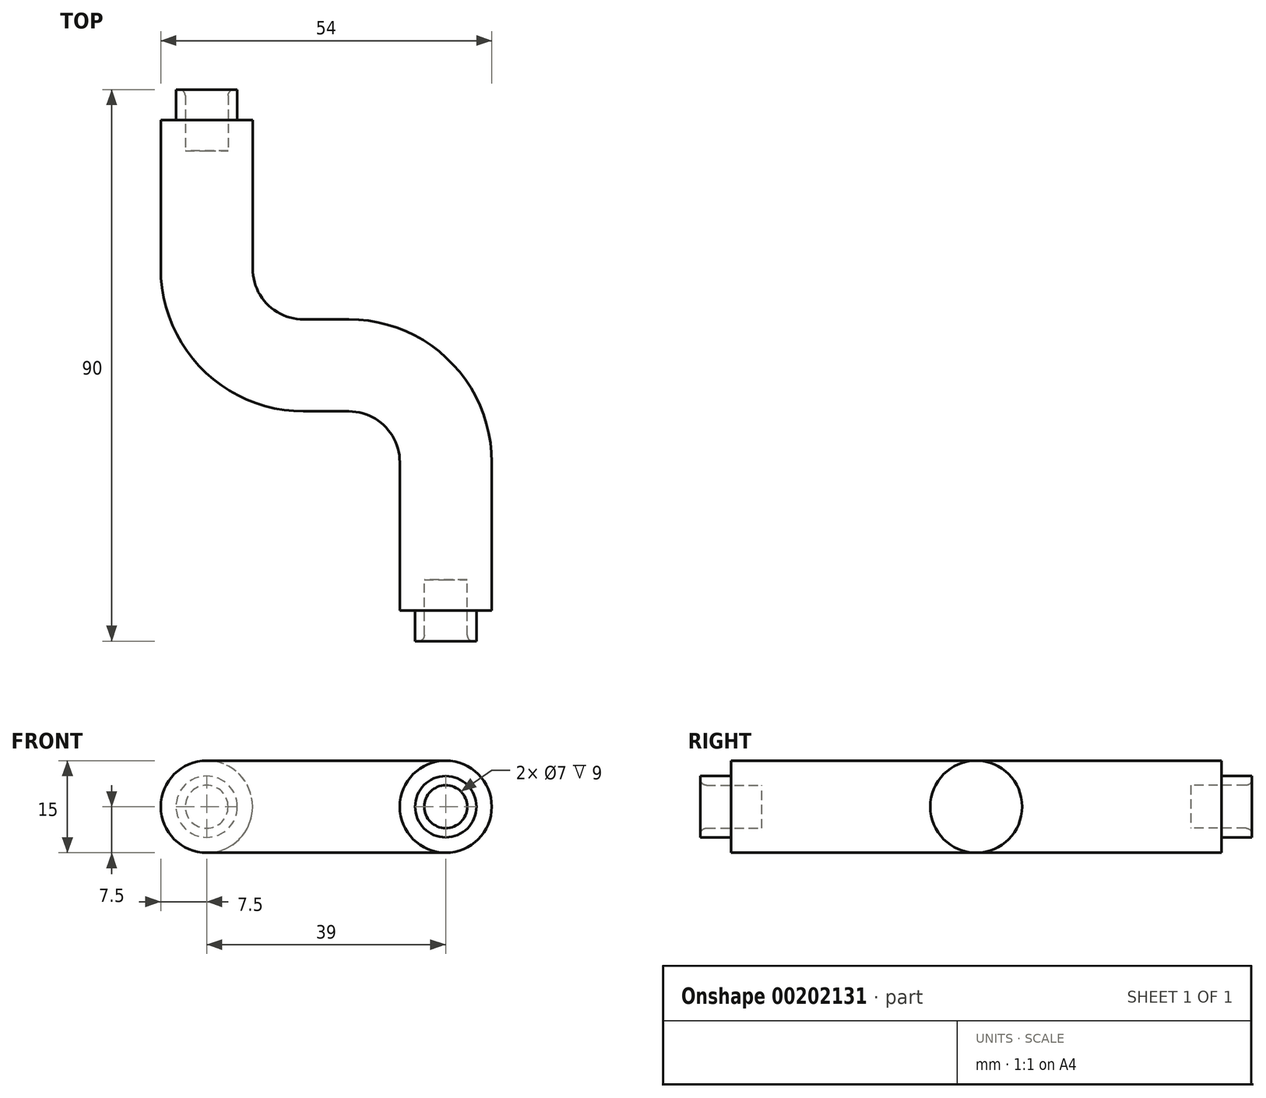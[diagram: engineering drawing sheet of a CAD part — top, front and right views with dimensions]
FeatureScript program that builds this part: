
annotation { "Feature Type Name" : "Feature", "Feature Type Description" : "" }
export const myFeature = defineFeature(function(context is Context, id is Id, definition is map)
    precondition{}
    {
        {
            var Q0;
            Q0=qCreatedBy(makeId("Top.planeOp"),FACE);
            var sketch = newSketch(context, id + "F0", { "sketchPlane" : qUnion([Q0])});
            skLineSegment(sketch, "E0", {"start": v(-15.8, 0) * mm, "end": v(-15.8, -24.2) * mm});
            skArc(sketch, "E1", {"start": v(-15.8, -24.2) * mm, "mid": v(-11.17, -35.37) * mm, "end": v(0, -40) * mm});
            skLineSegment(sketch, "E2", {"start": v(0, -40) * mm, "end": v(7.4, -40) * mm});
            skArc(sketch, "E3", {"start": v(23.2, -55.8) * mm, "mid": v(18.57, -44.63) * mm, "end": v(7.4, -40) * mm});
            skLineSegment(sketch, "E4", {"start": v(23.2, -55.8) * mm, "end": v(23.2, -80) * mm});
            skSolve(sketch);
        }
        {
            var Q0;
            Q0=qCreatedBy(makeId("Front.planeOp"),FACE);
            var sketch = newSketch(context, id + "F1", { "sketchPlane" : qUnion([Q0])});
            skCircle(sketch, "E5", {"center": v(-15.8, 0) * mm, "radius": 7.5 * mm});
            skSolve(sketch);
        }
        {
            var Q0;
            Q0=makeQuery(id+"F1.imprint","IMPRINT",FACE,{"disambiguationData":[TD([[makeQuery(id+"F1.imprint","IMPRINT",EDGE,{"derivedFrom":sQuery(id+"F1.wireOp",EDGE,"E5")}),1.0]])]});
            var Q1;
            Q1=sQuery(id+"F0.wireOp",EDGE,"E0");
            var Q2;
            Q2=sQuery(id+"F0.wireOp",EDGE,"E1");
            var Q3;
            Q3=sQuery(id+"F0.wireOp",EDGE,"E2");
            var Q4;
            Q4=sQuery(id+"F0.wireOp",EDGE,"E3");
            var Q5;
            Q5=sQuery(id+"F0.wireOp",EDGE,"E4");
            sweep(context, id + "F2", {"profiles" : qUnion([Q0]), "path" : qUnion([Q1, Q2, Q3, Q4, Q5])});
        }
        {
            var Q0;
            Q0=makeQuery(id+"F2.opSweep","CAP_FACE",FACE,{"disambiguationData":[OSD([sQuery(id+"F0.wireOp",VERTEX,"E4.end"),sQuery(id+"F1.wireOp",EDGE,"E5")])],"isStart":false});
            var sketch = newSketch(context, id + "F3", { "sketchPlane" : qUnion([Q0])});
            skCircle(sketch, "E6", {"center": v(23.2, 0) * mm, "radius": 3.5 * mm});
            skCircle(sketch, "E7", {"center": v(23.2, 0) * mm, "radius": 5 * mm});
            skSolve(sketch);
        }
        {
            var Q0;
            Q0 = qSketchRegion(id + "F3", true);
            extrude(context, id + "F4", {"entities" : qUnion([Q0]), "operationType" : NewBodyOperationType.ADD, "depth" : 5 * mm});
        }
        {
            var Q0;
            Q0=makeQuery(id+"F2.opSweep","CAP_FACE",FACE,{"disambiguationData":[OSD([sQuery(id+"F0.wireOp",VERTEX,"E0.start"),sQuery(id+"F1.wireOp",EDGE,"E5")])],"isStart":true});
            var sketch = newSketch(context, id + "F5", { "sketchPlane" : qUnion([Q0])});
            skCircle(sketch, "E8", {"center": v(15.8, 0) * mm, "radius": 3.5 * mm});
            skCircle(sketch, "E9", {"center": v(15.8, 0) * mm, "radius": 5 * mm});
            skSolve(sketch);
        }
        {
            var Q0;
            Q0 = qSketchRegion(id + "F5", true);
            extrude(context, id + "F6", {"entities" : qUnion([Q0]), "operationType" : NewBodyOperationType.ADD, "depth" : 5 * mm});
        }
        {
            var Q0;
            Q0=makeQuery(id+"F6.boolean.opBoolean","SPLIT",FACE,{"disambiguationData":[TD([makeQuery(id+"F6.opExtrude","SWEPT_FACE",FACE,{"disambiguationData":[OSD([sQuery(id+"F5.wireOp",EDGE,"E8")])]})])],"derivedFrom":makeQuery(id+"F2.opSweep","CAP_FACE",FACE,{"disambiguationData":[OSD([sQuery(id+"F0.wireOp",VERTEX,"E0.start"),sQuery(id+"F1.wireOp",EDGE,"E5")])],"isStart":true})});
            var sketch = newSketch(context, id + "F7", { "sketchPlane" : qUnion([Q0])});
            skCircle(sketch, "E10", {"center": v(15.8, 0) * mm, "radius": 3.5 * mm});
            skSolve(sketch);
        }
        {
            var Q0;
            Q0 = qSketchRegion(id + "F7", true);
            extrude(context, id + "F8", {"entities" : qUnion([Q0]), "operationType" : NewBodyOperationType.REMOVE, "oppositeDirection" : true, "depth" : 5 * mm});
        }
        {
            var Q0;
            Q0=makeQuery(id+"F4.boolean.opBoolean","SPLIT",FACE,{"disambiguationData":[TD([makeQuery(id+"F4.opExtrude","SWEPT_FACE",FACE,{"disambiguationData":[OSD([sQuery(id+"F3.wireOp",EDGE,"E6")])]})])],"derivedFrom":makeQuery(id+"F2.opSweep","CAP_FACE",FACE,{"disambiguationData":[OSD([sQuery(id+"F0.wireOp",VERTEX,"E4.end"),sQuery(id+"F1.wireOp",EDGE,"E5")])],"isStart":false})});
            var sketch = newSketch(context, id + "F9", { "sketchPlane" : qUnion([Q0])});
            skCircle(sketch, "E11", {"center": v(23.2, 0) * mm, "radius": 3.5 * mm});
            skSolve(sketch);
        }
        {
            var Q0;
            Q0 = qSketchRegion(id + "F9", true);
            extrude(context, id + "F10", {"entities" : qUnion([Q0]), "operationType" : NewBodyOperationType.REMOVE, "oppositeDirection" : true, "depth" : 5 * mm});
        }
        {
            var Q0;
            Q0=makeQuery(id+"F6.opExtrude","CAP_EDGE",EDGE,{"disambiguationData":[OSD([sQuery(id+"F5.wireOp",EDGE,"E8")])],"isStart":false});
            var Q1;
            Q1=makeQuery(id+"F4.opExtrude","CAP_EDGE",EDGE,{"disambiguationData":[OSD([sQuery(id+"F3.wireOp",EDGE,"E6")])],"isStart":false});
            fillet(context, id + "F11", {"entities" : qUnion([Q0, Q1]), "radius" : 1 * mm, "tangentPropagation" : true, "allowEdgeOverflow" : false});
        }
    });
